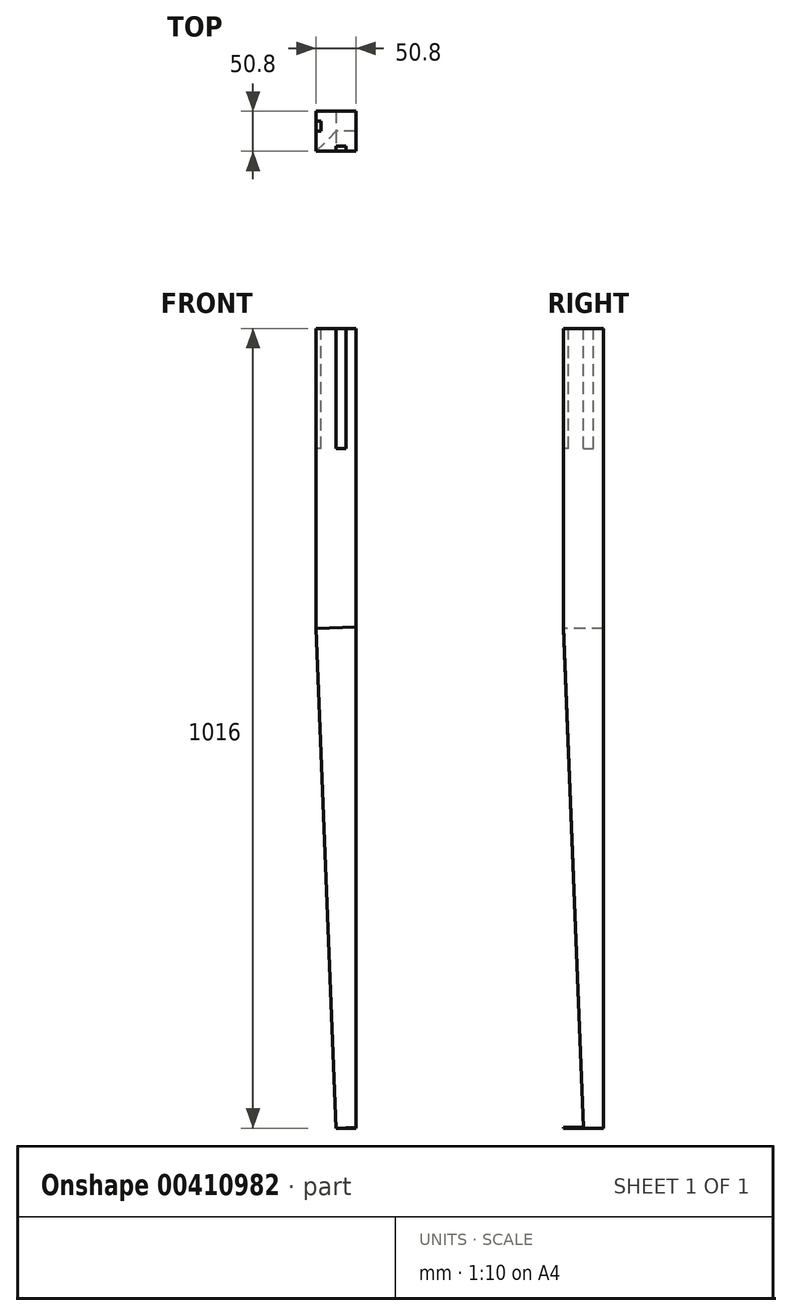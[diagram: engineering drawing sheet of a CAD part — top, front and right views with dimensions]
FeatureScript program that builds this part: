
annotation { "Feature Type Name" : "Feature", "Feature Type Description" : "" }
export const myFeature = defineFeature(function(context is Context, id is Id, definition is map)
    precondition{}
    {
        {
            var Q0;
            Q0=qCreatedBy(makeId("Front.planeOp"),FACE);
            var sketch = newSketch(context, id + "F0", { "sketchPlane" : qUnion([Q0])});
            skLineSegment(sketch, "E0", {"start": v(0, 0) * mm, "end": v(0, -1016) * mm});
            skLineSegment(sketch, "E1", {"start": v(0, -1016) * mm, "end": v(-25.4, -1016) * mm});
            skLineSegment(sketch, "E2", {"start": v(-25.4, -1016) * mm, "end": v(-50.8, -381) * mm});
            skLineSegment(sketch, "E3", {"start": v(-50.8, -381) * mm, "end": v(-50.8, 0) * mm});
            skLineSegment(sketch, "E4", {"start": v(-50.8, 0) * mm, "end": v(0, 0) * mm});
            skSolve(sketch);
        }
        {
            var Q0;
            Q0 = qSketchRegion(id + "F0", true);
            extrude(context, id + "F1", {"entities" : qUnion([Q0]), "oppositeDirection" : true, "depth" : 50.8 * mm});
        }
        {
            var Q0;
            Q0=makeQuery(id+"F1.opExtrude","SWEPT_FACE",FACE,{"disambiguationData":[OSD([sQuery(id+"F0.wireOp",EDGE,"E3")])]});
            var sketch = newSketch(context, id + "F2", { "sketchPlane" : qUnion([Q0])});
            skPoint(sketch, "E5.firstSnap0", {"position": v(-25.4, 0) * mm});
            skLineSegment(sketch, "E5.bottom", {"start": v(-25.4, -152.4) * mm, "end": v(-38.1, -152.4) * mm});
            skLineSegment(sketch, "E5.top", {"start": v(-25.4, 0) * mm, "end": v(-38.1, 0) * mm});
            skLineSegment(sketch, "E5.left", {"start": v(-25.4, -152.4) * mm, "end": v(-25.4, 0) * mm});
            skLineSegment(sketch, "E5.right", {"start": v(-38.1, -152.4) * mm, "end": v(-38.1, 0) * mm});
            skSolve(sketch);
        }
        {
            var Q0;
            Q0 = qSketchRegion(id + "F2", true);
            extrude(context, id + "F3", {"entities" : qUnion([Q0]), "operationType" : NewBodyOperationType.REMOVE, "oppositeDirection" : true, "depth" : 6.35 * mm});
        }
        {
            var Q0;
            Q0=makeQuery(id+"F1.opExtrude","SWEPT_FACE",FACE,{"disambiguationData":[OSD([sQuery(id+"F0.wireOp",EDGE,"E2")])]});
            var sketch = newSketch(context, id + "F4", { "sketchPlane" : qUnion([Q0])});
            skLineSegment(sketch, "E6", {"start": v(0, -378.67) * mm, "end": v(-25.4, -1014.17) * mm});
            skLineSegment(sketch, "E7", {"start": v(-25.4, -1014.17) * mm, "end": v(0, -1014.17) * mm});
            skLineSegment(sketch, "E8", {"start": v(0, -1014.17) * mm, "end": v(0, -378.67) * mm});
            skSolve(sketch);
        }
        {
            var Q0;
            Q0 = qSketchRegion(id + "F4", true);
            extrude(context, id + "F5", {"entities" : qUnion([Q0]), "operationType" : NewBodyOperationType.REMOVE, "endBound" : BoundingType.THROUGH_ALL, "oppositeDirection" : true, "depth" : 25.4 * mm});
        }
        {
            var Q0;
            {var subQ0=sQuery(id+"F0.wireOp",EDGE,"E4");var subQ1=sQuery(id+"F0.wireOp",EDGE,"E2");var subQ2=sQuery(id+"F0.wireOp",EDGE,"E3");var subQ3=sQuery(id+"F0.wireOp",EDGE,"E0");Q0=makeQuery(id+"F5.boolean.opBoolean","SPLIT",FACE,{"disambiguationData":[TD([makeQuery(id+"F1.opExtrude","SWEPT_FACE",FACE,{"disambiguationData":[OSD([subQ1])]})])],"derivedFrom":makeQuery(id+"F1.opExtrude","CAP_FACE",FACE,{"disambiguationData":[OSD([subQ3,sQuery(id+"F0.wireOp",EDGE,"E1"),subQ1,subQ2,subQ0])],"isStart":true})});}
            var sketch = newSketch(context, id + "F6", { "sketchPlane" : qUnion([Q0])});
            skLineSegment(sketch, "E9.bottom", {"start": v(-12.7, -152.4) * mm, "end": v(-25.4, -152.4) * mm});
            skLineSegment(sketch, "E9.top", {"start": v(-12.7, 0) * mm, "end": v(-25.4, 0) * mm});
            skLineSegment(sketch, "E9.left", {"start": v(-12.7, -152.4) * mm, "end": v(-12.7, 0) * mm});
            skLineSegment(sketch, "E9.right", {"start": v(-25.4, -152.4) * mm, "end": v(-25.4, 0) * mm});
            skSolve(sketch);
        }
        {
            var Q0;
            Q0 = qSketchRegion(id + "F6", true);
            var Q1;
            Q1=makeQuery(id+"F6.imprint","IMPRINT",FACE,{"disambiguationData":[TD([[makeQuery(id+"F6.imprint","IMPRINT",EDGE,{"derivedFrom":sQuery(id+"F6.wireOp",EDGE,"E9.bottom")}),-1.0]])]});
            extrude(context, id + "F7", {"entities" : qUnion([Q0, Q1]), "operationType" : NewBodyOperationType.REMOVE, "oppositeDirection" : true, "depth" : 6.35 * mm});
        }
    });
